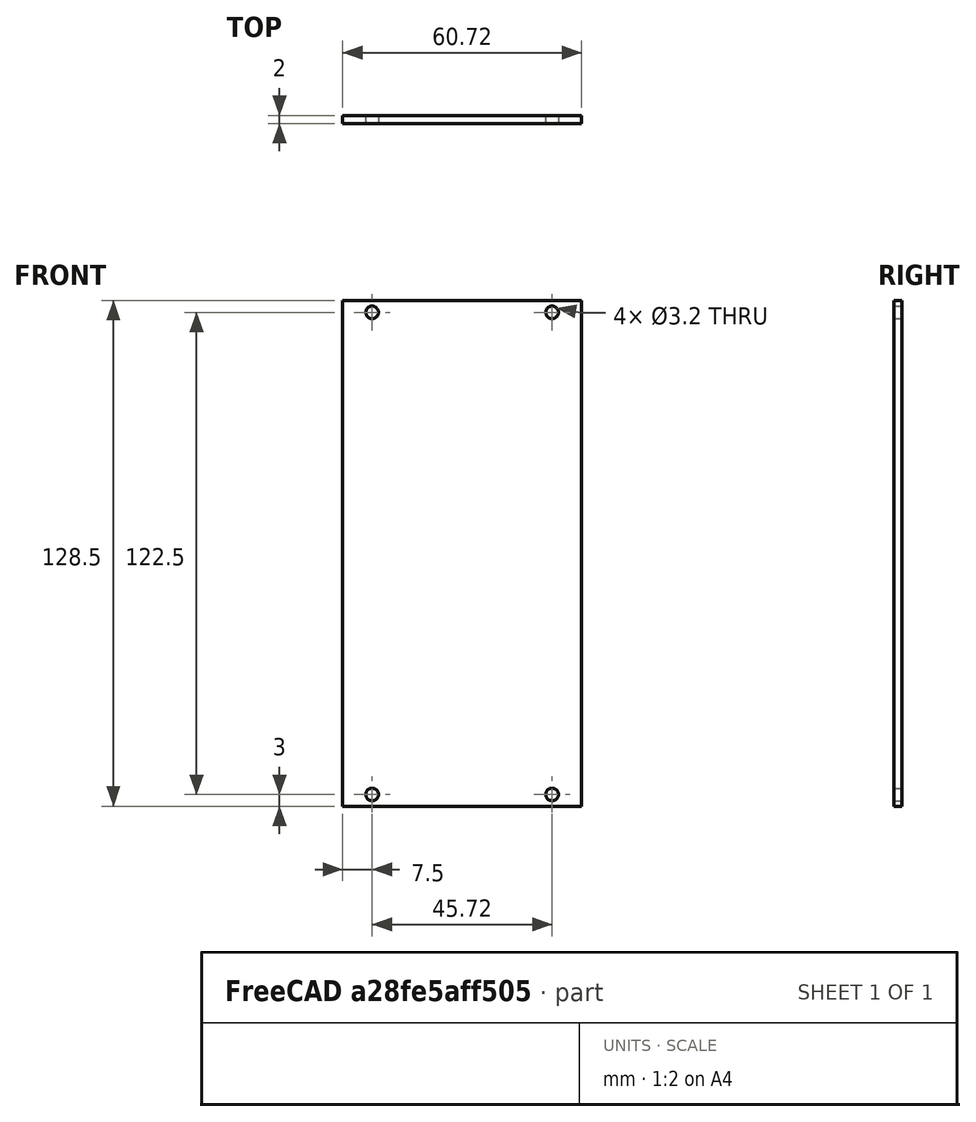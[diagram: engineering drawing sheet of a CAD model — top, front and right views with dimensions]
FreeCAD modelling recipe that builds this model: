
FCSTD DOCUMENT  (FreeCAD 1.0R38641 +468 (Git))
Label: 12hp_plate
License: All rights reserved
LicenseURL: https://en.wikipedia.org/wiki/All_rights_reserved
objects: Sketcher::SketchObject×1, PartDesign::Pad×1, PartDesign::Body×1, App::VarSet×1
note: 6 computed .brp shape members not serialized (recipe doc carries the construction recipe); baked Part::Feature solids carry a one-line shape summary decoded from their .brp
EXTERNAL_REF file=plate_dims.FCStd obj=VarSet

FEATURE [Sketcher::SketchObject] Sketch
  ArcFitTolerance = 1e-06
  AttachmentSupport = -> [XZ_Plane]
  FullyConstrained = true
  MakeInternals = false
  MapMode = 5
  Placement = pos=(0,0,0) rot=(1,0,0;1.5708rad)
  expr: Constraints[39] = <<plate_dims>>#VarSet.HoleOffsetY
  expr: Constraints[40] = <<plate_dims>>#VarSet.HoleOffsetX
  expr: Constraints[48] = <<plate_dims>>#VarSet.HoleDiameter
  expr: Constraints[49] = <<plate_dims>>#VarSet.PlateHeight
  expr: Constraints[52] = <<plate_dims>>#VarSet.HoleSpacing * (VarSet.PlateWidthHP - 3)
  sketch-geometry (20):
    g0: LineSegment StartX=-30.36 StartY=64.25 StartZ=0 EndX=-30.36 EndY=-64.25 EndZ=0
    g1: LineSegment StartX=-30.36 StartY=-64.25 StartZ=0 EndX=30.36 EndY=-64.25 EndZ=0
    g2: LineSegment StartX=30.36 StartY=-64.25 StartZ=0 EndX=30.36 EndY=64.25 EndZ=0
    g3: LineSegment StartX=30.36 StartY=64.25 StartZ=0 EndX=-30.36 EndY=64.25 EndZ=0
    g4: LineSegment [constr] StartX=22.86 StartY=61.25 StartZ=0 EndX=30.36 EndY=61.25 EndZ=0
    g5: LineSegment [constr] StartX=22.86 StartY=64.25 StartZ=0 EndX=22.86 EndY=61.25 EndZ=0
    g6: LineSegment [constr] StartX=22.86 StartY=61.25 StartZ=0 EndX=22.86 EndY=-61.25 EndZ=0
    g7: LineSegment [constr] StartX=22.86 StartY=-61.25 StartZ=0 EndX=22.86 EndY=-64.25 EndZ=0
    g8: LineSegment [constr] StartX=22.86 StartY=-61.25 StartZ=0 EndX=30.36 EndY=-61.25 EndZ=0
    g9: LineSegment [constr] StartX=-22.86 StartY=-61.25 StartZ=0 EndX=-22.86 EndY=-64.25 EndZ=0
    g10: LineSegment [constr] StartX=-30.36 StartY=-61.25 StartZ=0 EndX=-22.86 EndY=-61.25 EndZ=0
    g11: LineSegment [constr] StartX=-22.86 StartY=-61.25 StartZ=0 EndX=22.86 EndY=-61.25 EndZ=0
    g12: LineSegment [constr] StartX=-30.36 StartY=61.25 StartZ=0 EndX=-22.86 EndY=61.25 EndZ=0
    g13: LineSegment [constr] StartX=-22.86 StartY=61.25 StartZ=0 EndX=22.86 EndY=61.25 EndZ=0
    g14: LineSegment [constr] StartX=-22.86 StartY=64.25 StartZ=0 EndX=-22.86 EndY=61.25 EndZ=0
    g15: LineSegment [constr] StartX=-22.86 StartY=61.25 StartZ=0 EndX=-22.86 EndY=-61.25 EndZ=0
    g16: Circle CenterX=-22.86 CenterY=61.25 CenterZ=0 NormalX=0 NormalY=0 NormalZ=1 AngleXU=0 Radius=1.6
    g17: Circle CenterX=22.86 CenterY=61.25 CenterZ=0 NormalX=0 NormalY=0 NormalZ=1 AngleXU=0 Radius=1.6
    g18: Circle CenterX=22.86 CenterY=-61.25 CenterZ=0 NormalX=0 NormalY=0 NormalZ=1 AngleXU=0 Radius=1.6
    g19: Circle CenterX=-22.86 CenterY=-61.25 CenterZ=0 NormalX=0 NormalY=0 NormalZ=1 AngleXU=0 Radius=1.6
  constraints (58):
    c: Coincident(g0,g1)
    c: Coincident(g1,g2)
    c: Coincident(g2,g3)
    c: Coincident(g3,g0)
    c: Vertical(g2)
    c: Horizontal(g1)
    c: PointOnObject(g14,g3)
    c: PointOnObject(g9,g1)
    c: PointOnObject(g12,g0)
    c: PointOnObject(g4,g2)
    c: PointOnObject(g10,g0)
    c: PointOnObject(g8,g2)
    c: PointOnObject(g5,g3)
    c: PointOnObject(g7,g1)
    c: Coincident(g13,g4)
    c: Horizontal(g4)
    c: Coincident(g5,g6)
    c: Vertical(g5)
    c: Coincident(g6,g7)
    c: Vertical(g6)
    c: Vertical(g7)
    c: Coincident(g11,g8)
    c: Horizontal(g8)
    c: Coincident(g15,g9)
    c: Vertical(g9)
    c: Coincident(g10,g11)
    c: Horizontal(g10)
    c: Horizontal(g11)
    c: Coincident(g12,g13)
    c: Horizontal(g12)
    c: Horizontal(g13)
    c: Coincident(g14,g15)
    c: Vertical(g14)
    c: Vertical(g15)
    c: Coincident(g12,g14)
    c: Coincident(g9,g10)
    c: Coincident(g8,g6)
    c: Coincident(g4,g5)
    c: Equal(g9,g14)
    c: Distance(g9,g9) = 3
    c: Distance(g10,g10) = 7.5
    c: Coincident(g16,g12)
    c: Coincident(g17,g4)
    c: Coincident(g18,g6)
    c: Coincident(g19,g9)
    c: Equal(g19,g18)
    c: Equal(g18,g17)
    c: Equal(g17,g16)
    c: Diameter(g16) = 3.2
    c: DistanceY(g0,g0) = 128.5
    c: Distance(g12,g9) = 125.5
    c: Distance(g14,g14) = 3
    c: Distance(g11,g11) = 45.72
    c: Distance(g1,g1) = 60.72
    c: Symmetric(g0,g2,g-2)
    c: Symmetric(g0,g0,g-1)
    c: Distance(g8,g8) = 7.5
    c: Equal(g8,g10)
FEATURE [PartDesign::Pad] Pad
  Direction = (0,-1,2e-16)
  Length = 2
  Length2 = 10
  Placement = pos=(0,0,0) rot=(1,0,0;1.5708rad)
  Profile = -> Sketch
  ReferenceAxis = -> Sketch [N_Axis]
  Refine = true
  Suppressed = false
  Type = 0
FEATURE [PartDesign::Body] Body  label="12HpPlate"
  AllowCompound = false
  Group = -> [Sketch,Pad]
  Origin = -> Origin
  Tip = -> Pad
FEATURE [App::VarSet] VarSet
  PlateWidthHP = 12
